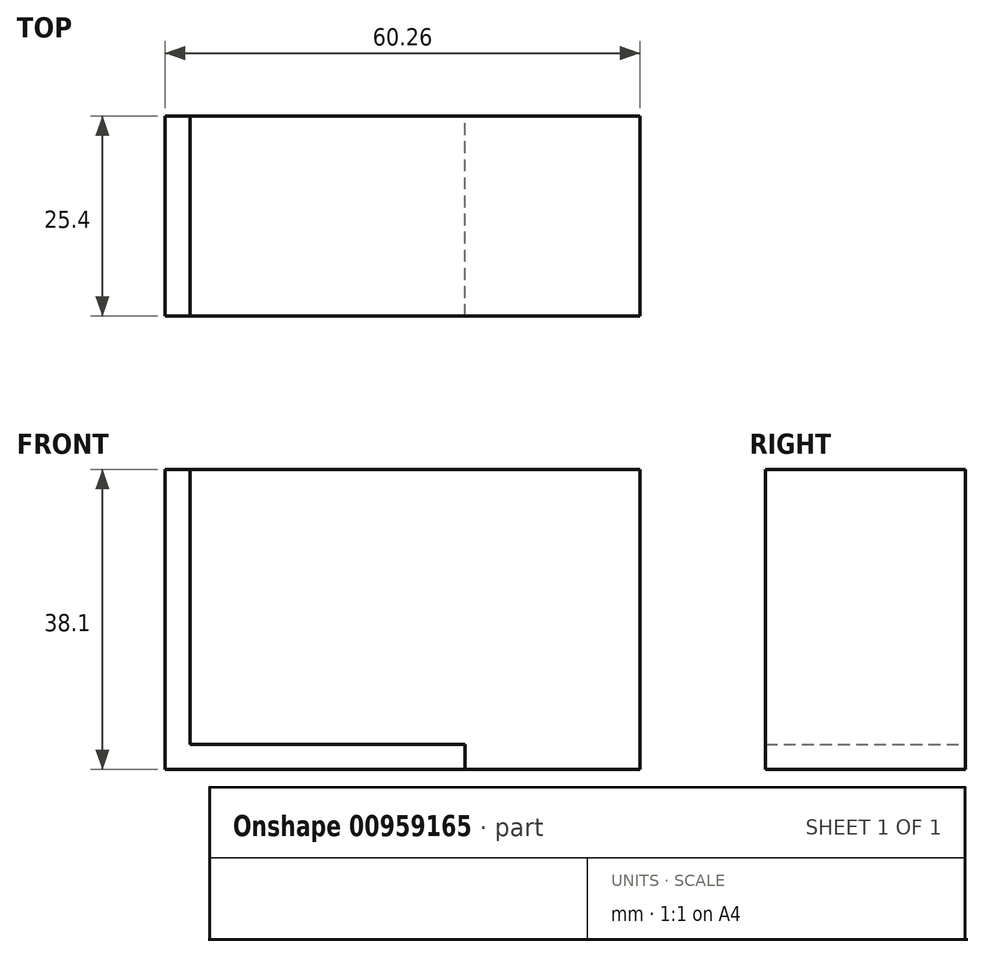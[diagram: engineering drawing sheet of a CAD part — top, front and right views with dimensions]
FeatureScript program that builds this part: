
annotation { "Feature Type Name" : "Feature", "Feature Type Description" : "" }
export const myFeature = defineFeature(function(context is Context, id is Id, definition is map)
    precondition{}
    {
        {
            var Q0;
            Q0=qCreatedBy(makeId("Front.planeOp"),FACE);
            var sketch = newSketch(context, id + "F0", { "sketchPlane" : qUnion([Q0])});
            skLineSegment(sketch, "E0", {"start": v(0, 0) * mm, "end": v(-60.26, 0) * mm});
            skLineSegment(sketch, "E1", {"start": v(-60.26, 0) * mm, "end": v(-60.26, 38.1) * mm});
            skLineSegment(sketch, "E2", {"start": v(-60.26, 38.1) * mm, "end": v(0, 38.1) * mm});
            skLineSegment(sketch, "E3", {"start": v(0, 38.1) * mm, "end": v(0, 0) * mm});
            skLineSegment(sketch, "E4", {"start": v(-57.09, 3.17) * mm, "end": v(-57.09, 38.1) * mm});
            skLineSegment(sketch, "E5", {"start": v(-57.09, 3.17) * mm, "end": v(-22.16, 3.17) * mm});
            skLineSegment(sketch, "E6", {"start": v(-22.16, 3.17) * mm, "end": v(-22.16, 0) * mm});
            skPoint(sketch, "E7.orphan", {"position": v(-57.09, 0) * mm});
            skSolve(sketch);
        }
        {
            var Q0;
            {var subQ1=sQuery(id+"F0.wireOp",EDGE,"E1");Q0=makeQuery(id+"F0.imprint","IMPRINT",FACE,{"disambiguationData":[TD([[makeQuery(id+"F0.imprint","IMPRINT",EDGE,{"derivedFrom":subQ1}),-1.0]])]});}
            extrude(context, id + "F1", {"entities" : qUnion([Q0]), "depth" : 25.4 * mm, "offsetDistance" : 25.4 * mm});
        }
        {
            var Q0;
            {var subQ1=sQuery(id+"F0.wireOp",EDGE,"E3");Q0=makeQuery(id+"F0.imprint","IMPRINT",FACE,{"disambiguationData":[TD([[makeQuery(id+"F0.imprint","IMPRINT",EDGE,{"derivedFrom":subQ1}),-1.0]])]});}
            extrude(context, id + "F2", {"entities" : qUnion([Q0]), "depth" : 25.4 * mm, "offsetDistance" : 25.4 * mm});
        }
    });
